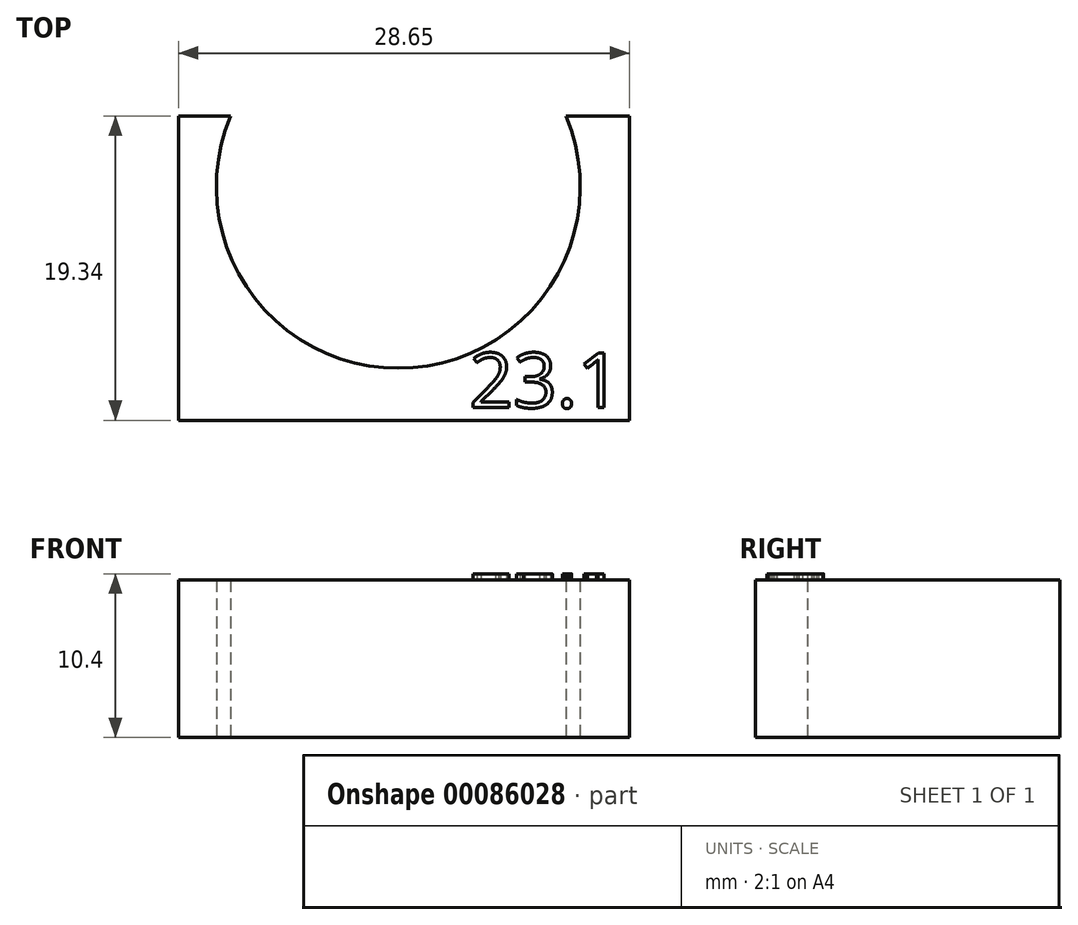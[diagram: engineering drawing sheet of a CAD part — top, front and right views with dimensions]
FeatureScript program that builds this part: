
annotation { "Feature Type Name" : "Feature", "Feature Type Description" : "" }
export const myFeature = defineFeature(function(context is Context, id is Id, definition is map)
    precondition{}
    {
        {
            var Q0;
            Q0=qCreatedBy(makeId("Top.planeOp"),FACE);
            var sketch = newSketch(context, id + "F0", { "sketchPlane" : qUnion([Q0])});
            skCircle(sketch, "E0", {"center": v(0, 0) * mm, "radius": 11.55 * mm});
            skLineSegment(sketch, "E1.bottom", {"start": v(-13.97, 4.48) * mm, "end": v(14.68, 4.48) * mm});
            skLineSegment(sketch, "E1.top", {"start": v(-13.97, -14.86) * mm, "end": v(14.68, -14.86) * mm});
            skLineSegment(sketch, "E1.left", {"start": v(-13.97, 4.48) * mm, "end": v(-13.97, -14.86) * mm});
            skLineSegment(sketch, "E1.right", {"start": v(14.68, 4.48) * mm, "end": v(14.68, -14.86) * mm});
            skSolve(sketch);
        }
        {
            var Q0;
            Q0=makeQuery(id+"F0.imprint","IMPRINT",FACE,{"disambiguationData":[TD([[makeQuery(id+"F0.imprint","IMPRINT",EDGE,{"derivedFrom":sQuery(id+"F0.wireOp",EDGE,"E0")}),-1.0]])]});
            extrude(context, id + "F1", {"entities" : qUnion([Q0]), "depth" : 10 * mm});
        }
        {
            var Q0;
            Q0=makeQuery(id+"F1.opExtrude","SWEPT_BODY",BODY,{"disambiguationData":[OSD([sQuery(id+"F0.wireOp",EDGE,"E0"),sQuery(id+"F0.wireOp",EDGE,"E1.bottom"),sQuery(id+"F0.wireOp",EDGE,"E1.top"),sQuery(id+"F0.wireOp",EDGE,"E1.left"),sQuery(id+"F0.wireOp",EDGE,"E1.right")])]});
            transform(context, id + "F2", {"entities" : qUnion([Q0]), "transformType" : TransformType.TRANSLATION_3D, "dx" : 0 * mm, "dy" : 0 * mm, "dz" : 0 * mm, "makeCopy" : true});
        }
        {
            var Q0;
            Q0=makeQuery(id+"F2.opPattern","COPY",BODY,{"derivedFrom":makeQuery(id+"F1.opExtrude","SWEPT_BODY",BODY,{"disambiguationData":[OSD([sQuery(id+"F0.wireOp",EDGE,"E0"),sQuery(id+"F0.wireOp",EDGE,"E1.bottom"),sQuery(id+"F0.wireOp",EDGE,"E1.top"),sQuery(id+"F0.wireOp",EDGE,"E1.left"),sQuery(id+"F0.wireOp",EDGE,"E1.right")])]}),"instanceName":"1"});
            deleteBodies(context, id + "F3", {"entities" : qUnion([Q0])});
        }
        {
            var Q0;
            Q0=makeQuery(id+"F1.opExtrude","CAP_FACE",FACE,{"disambiguationData":[OSD([sQuery(id+"F0.wireOp",EDGE,"E0"),sQuery(id+"F0.wireOp",EDGE,"E1.bottom"),sQuery(id+"F0.wireOp",EDGE,"E1.top"),sQuery(id+"F0.wireOp",EDGE,"E1.left"),sQuery(id+"F0.wireOp",EDGE,"E1.right")])],"isStart":false});
            var sketch = newSketch(context, id + "F4", { "sketchPlane" : qUnion([Q0])});
            skText(sketch, "E2", { "text": "23.1\n", "fontName": "OpenSans-Regular.ttf"});
            const initialGuessF4  = {"E2": [0.00451, -0.01405, 1, 0, 0.0035]};
            skSetInitialGuess(sketch, initialGuessF4);
            skSolve(sketch);
        }
        {
            var Q0;
            Q0 = qSketchRegion(id + "F4", true);
            extrude(context, id + "F5", {"entities" : qUnion([Q0]), "operationType" : NewBodyOperationType.ADD, "depth" : .4 * mm});
        }
    });
